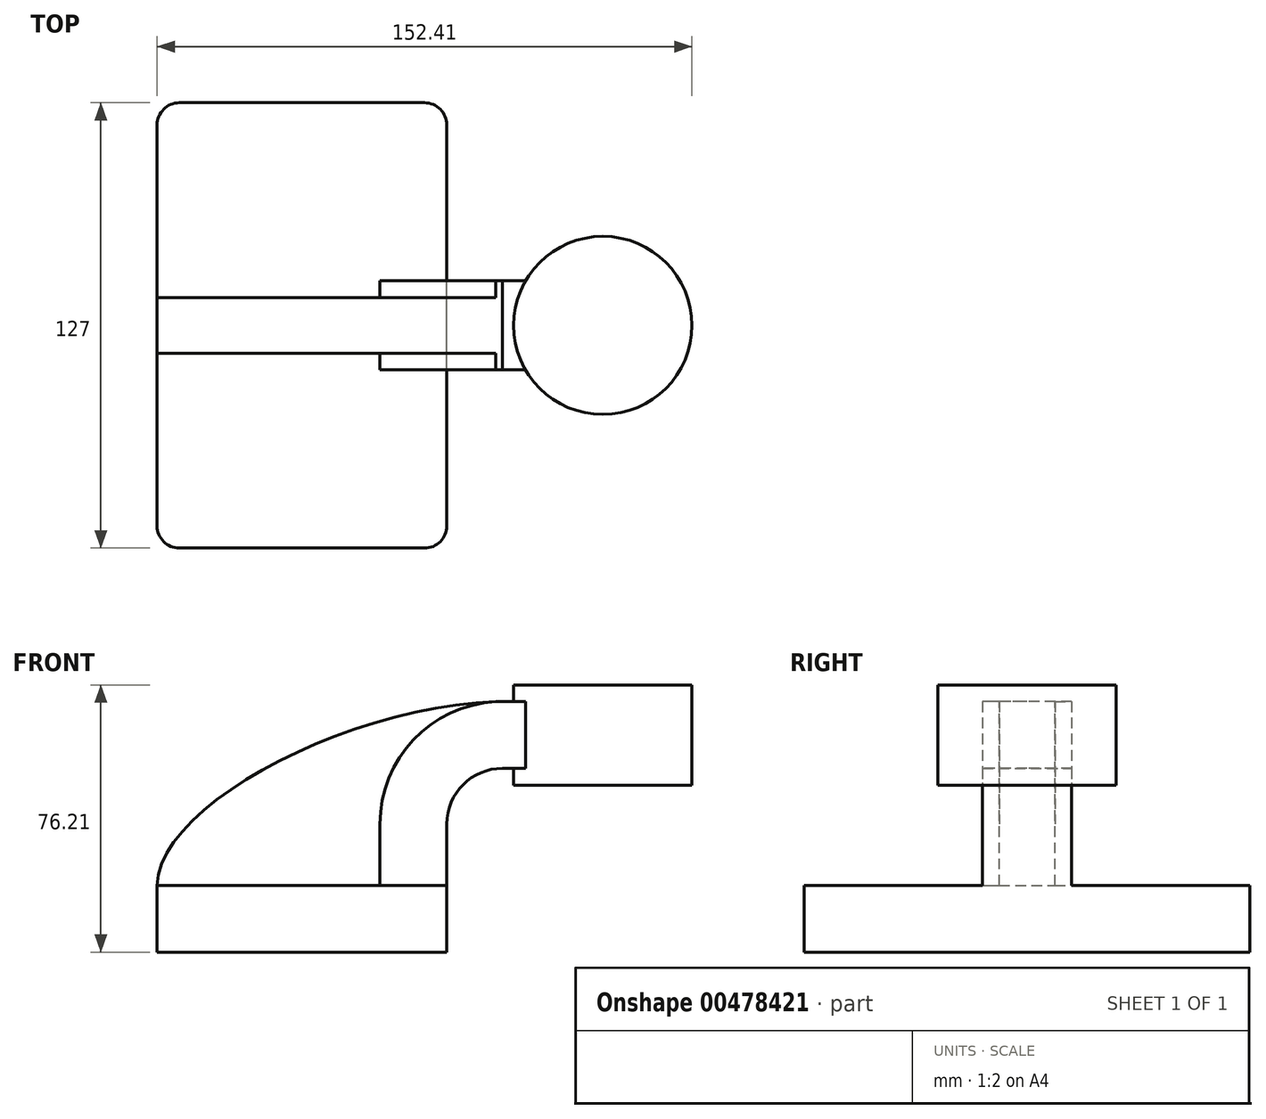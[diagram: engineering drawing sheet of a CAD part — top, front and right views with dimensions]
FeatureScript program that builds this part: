
annotation { "Feature Type Name" : "Feature", "Feature Type Description" : "" }
export const myFeature = defineFeature(function(context is Context, id is Id, definition is map)
    precondition{}
    {
        {
            var Q0;
            Q0=qCreatedBy(makeId("Front.planeOp"),FACE);
            var sketch = newSketch(context, id + "F0", { "sketchPlane" : qUnion([Q0])});
            skLineSegment(sketch, "E0.bottom", {"start": v(-41.28, 9.52) * mm, "end": v(41.27, 9.53) * mm});
            skLineSegment(sketch, "E0.top", {"start": v(-41.28, -9.53) * mm, "end": v(41.28, -9.53) * mm});
            skLineSegment(sketch, "E0.left", {"start": v(-41.28, 9.52) * mm, "end": v(-41.27, -9.53) * mm});
            skLineSegment(sketch, "E0.right", {"start": v(41.28, 9.53) * mm, "end": v(41.28, -9.52) * mm});
            skPoint(sketch, "E0.middle", {"position": v(0, 0) * mm});
            skLineSegment(sketch, "E1.bottom", {"start": v(60.32, 38.1) * mm, "end": v(111.12, 38.1) * mm});
            skLineSegment(sketch, "E1.top", {"start": v(60.32, 66.68) * mm, "end": v(111.12, 66.68) * mm});
            skLineSegment(sketch, "E1.left", {"start": v(60.32, 38.1) * mm, "end": v(60.32, 66.68) * mm});
            skLineSegment(sketch, "E1.right", {"start": v(111.12, 38.1) * mm, "end": v(111.12, 66.68) * mm});
            skPoint(sketch, "E1.middle", {"position": v(85.72, 52.39) * mm});
            skLineSegment(sketch, "E2", {"start": v(41.27, 9.53) * mm, "end": v(41.27, 27) * mm});
            skArc(sketch, "E3", {"start": v(41.27, 27) * mm, "mid": v(45.92, 38.23) * mm, "end": v(57.15, 42.88) * mm});
            skLineSegment(sketch, "E4", {"start": v(57.15, 42.88) * mm, "end": v(86.87, 42.88) * mm});
            skLineSegment(sketch, "E5.0", {"start": v(57.15, 61.93) * mm, "end": v(86.87, 61.93) * mm});
            skArc(sketch, "E5.1", {"start": v(22.22, 27) * mm, "mid": v(32.45, 51.7) * mm, "end": v(57.15, 61.93) * mm});
            skLineSegment(sketch, "E5.2", {"start": v(22.22, 9.53) * mm, "end": v(22.22, 27) * mm});
            skLineSegment(sketch, "E6", {"start": v(85.72, 38.1) * mm, "end": v(85.72, 66.68) * mm});
            skFitSpline(sketch, "E7", {"points": [v(-41.28, 9.52) * mm, v(57.15, 61.93) * mm], "startDerivative": vector(1.66, 69.85) * mm, "endDerivative": vector(129.58, 2.4) * mm});
            skSolve(sketch);
        }
        {
            var Q0;
            Q0=makeQuery(id+"F0.imprint","IMPRINT",FACE,{"disambiguationData":[TD([[makeQuery(id+"F0.imprint","IMPRINT",EDGE,{"derivedFrom":sQuery(id+"F0.wireOp",EDGE,"E0.top")}),1.0]])]});
            extrude(context, id + "F1", {"entities" : qUnion([Q0]), "endBound" : BoundingType.SYMMETRIC, "depth" : 127 * mm});
        }
        {
            var Q0;
            {var subQ0=sQuery(id+"F0.wireOp",EDGE,"E4");var subQ1=sQuery(id+"F0.wireOp",EDGE,"E1.left");var subQ2=makeQuery(id+"F0.imprint","INTERSECT",VERTEX,{"derivedFrom":[subQ1,subQ0]});Q0=makeQuery(id+"F0.imprint","IMPRINT",FACE,{"disambiguationData":[TD([[makeQuery(id+"F0.imprint","IMPRINT",EDGE,{"disambiguationData":[TD([[subQ2,-1.0]])],"derivedFrom":subQ1}),-1.0]])]});}
            var Q1;
            {var subQ1=sQuery(id+"F0.wireOp",EDGE,"E2");Q1=makeQuery(id+"F0.imprint","IMPRINT",FACE,{"disambiguationData":[TD([[makeQuery(id+"F0.imprint","IMPRINT",EDGE,{"derivedFrom":subQ1}),1.0]])]});}
            extrude(context, id + "F2", {"entities" : qUnion([Q0, Q1]), "operationType" : NewBodyOperationType.ADD, "endBound" : BoundingType.SYMMETRIC, "depth" : 25.4 * mm});
        }
        {
            var Q0;
            {var subQ3=sQuery(id+"F0.wireOp",EDGE,"E5.2");Q0=makeQuery(id+"F0.imprint","IMPRINT",FACE,{"disambiguationData":[TD([[makeQuery(id+"F0.imprint","IMPRINT",EDGE,{"derivedFrom":subQ3}),1.0]])]});}
            extrude(context, id + "F3", {"entities" : qUnion([Q0]), "operationType" : NewBodyOperationType.ADD, "endBound" : BoundingType.SYMMETRIC, "depth" : 15.88 * mm});
        }
        {
            var Q0;
            {var subQ4=sQuery(id+"F0.wireOp",EDGE,"E1.right");Q0=makeQuery(id+"F0.imprint","IMPRINT",FACE,{"disambiguationData":[TD([[makeQuery(id+"F0.imprint","IMPRINT",EDGE,{"derivedFrom":subQ4}),1.0]])]});}
            var Q1;
            Q1=sQuery(id+"F0.wireOp",EDGE,"E6");
            revolve(context, id + "F4", {"operationType" : NewBodyOperationType.ADD, "entities" : qUnion([Q0]), "axis" : qUnion([Q1]), "revolveType" : RevolveType.FULL});
        }
        {
            var Q0;
            Q0=makeQuery(id+"F1.opExtrude","CAP_EDGE",EDGE,{"disambiguationData":[OSD([sQuery(id+"F0.wireOp",EDGE,"E0.left")])],"isStart":false});
            var Q1;
            Q1=makeQuery(id+"F1.opExtrude","CAP_EDGE",EDGE,{"disambiguationData":[OSD([sQuery(id+"F0.wireOp",EDGE,"E0.right")])],"isStart":false});
            var Q2;
            Q2=makeQuery(id+"F1.opExtrude","CAP_EDGE",EDGE,{"disambiguationData":[OSD([sQuery(id+"F0.wireOp",EDGE,"E0.right")])],"isStart":true});
            var Q3;
            Q3=makeQuery(id+"F1.opExtrude","CAP_EDGE",EDGE,{"disambiguationData":[OSD([sQuery(id+"F0.wireOp",EDGE,"E0.left")])],"isStart":true});
            fillet(context, id + "F5", {"entities" : qUnion([Q0, Q1, Q2, Q3]), "radius" : 6.35 * mm, "tangentPropagation" : true, "allowEdgeOverflow" : false});
        }
    });
